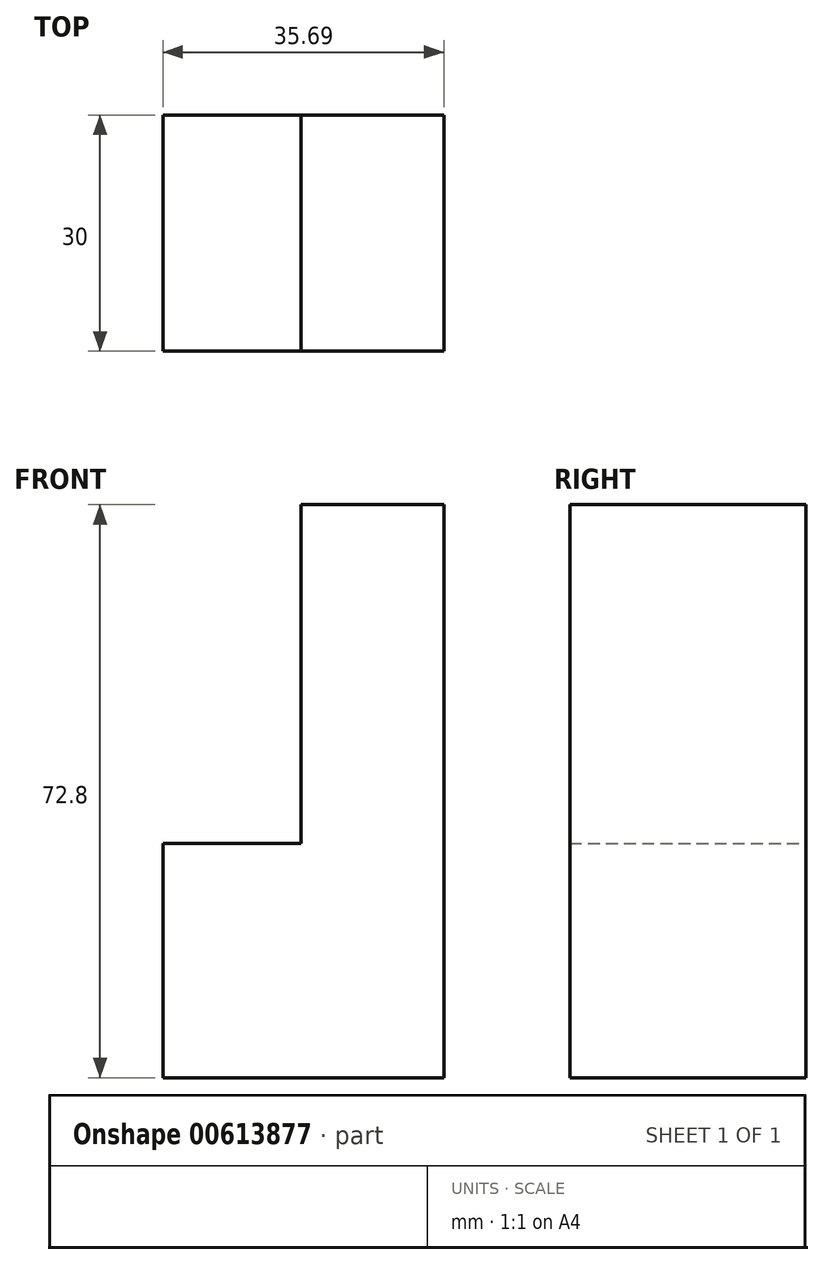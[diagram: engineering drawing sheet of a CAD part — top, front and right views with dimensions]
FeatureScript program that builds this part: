
annotation { "Feature Type Name" : "Feature", "Feature Type Description" : "" }
export const myFeature = defineFeature(function(context is Context, id is Id, definition is map)
    precondition{}
    {
        {
            var Q0;
            Q0=qCreatedBy(makeId("Front.planeOp"),FACE);
            var sketch = newSketch(context, id + "F0", { "sketchPlane" : qUnion([Q0])});
            skLineSegment(sketch, "E0", {"start": v(-12.6, 39.23) * mm, "end": v(-12.6, -33.57) * mm});
            skLineSegment(sketch, "E1", {"start": v(-12.6, -33.57) * mm, "end": v(-48.3, -33.57) * mm});
            skLineSegment(sketch, "E2", {"start": v(-48.3, -33.57) * mm, "end": v(-48.3, -3.82) * mm});
            skLineSegment(sketch, "E3", {"start": v(-48.3, -3.82) * mm, "end": v(-30.74, -3.82) * mm});
            skPoint(sketch, "E4.end.orphan", {"position": v(-30.74, 39.23) * mm});
            skPoint(sketch, "E5.start.orphan", {"position": v(-32.15, 39.23) * mm});
            skLineSegment(sketch, "E6", {"start": v(-12.6, 39.23) * mm, "end": v(-30.74, 39.23) * mm});
            skLineSegment(sketch, "E7", {"start": v(-30.74, -3.82) * mm, "end": v(-30.74, 39.23) * mm});
            skSolve(sketch);
        }
        {
            var Q0;
            Q0 = qSketchRegion(id + "F0", true);
            extrude(context, id + "F1", {"entities" : qUnion([Q0]), "depth" : 30 * mm, "offsetDistance" : 25 * mm});
        }
    });
